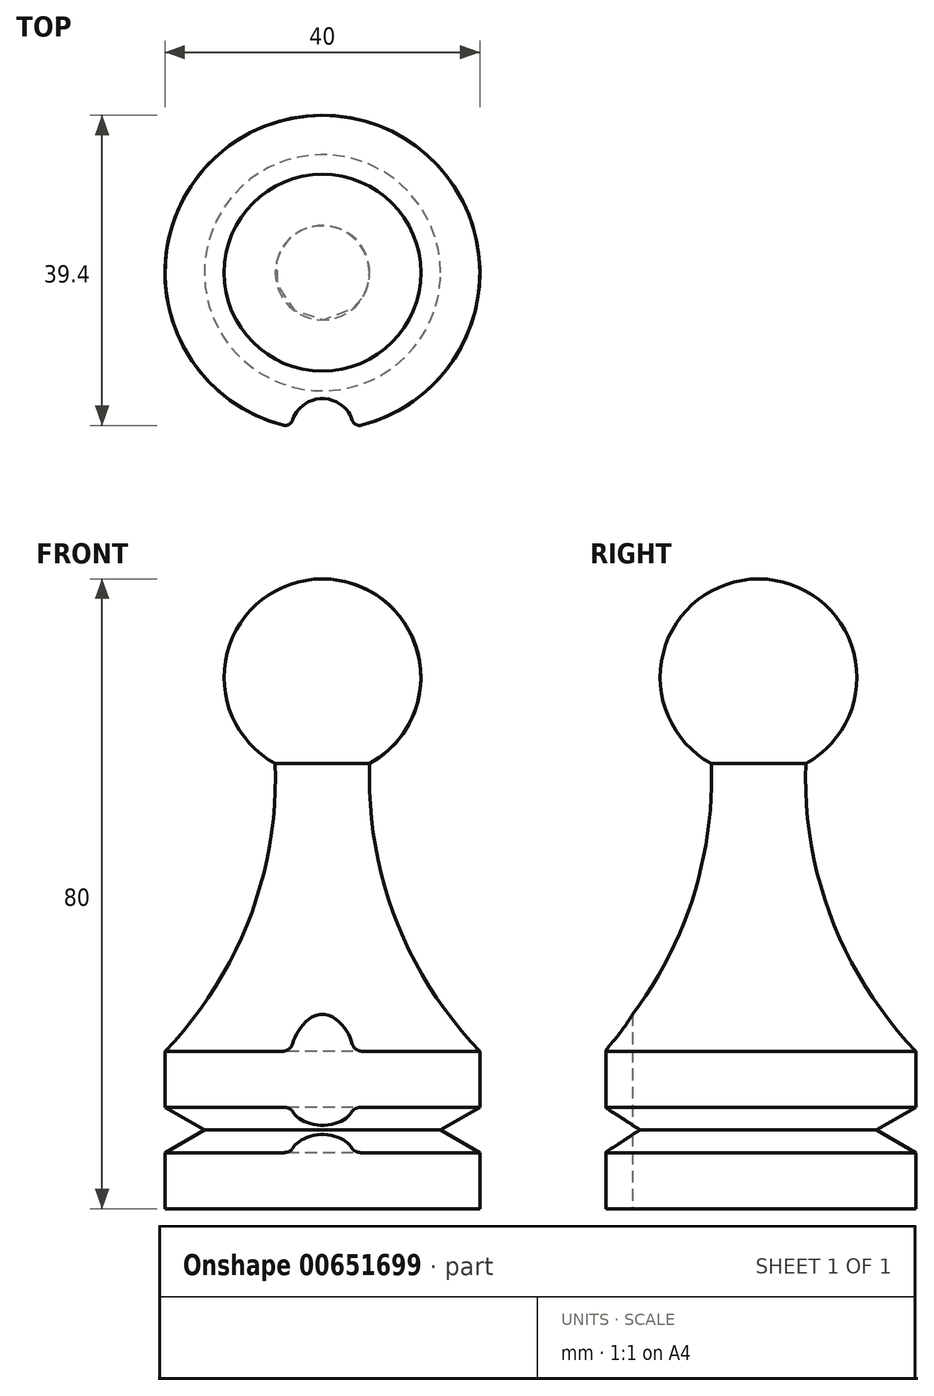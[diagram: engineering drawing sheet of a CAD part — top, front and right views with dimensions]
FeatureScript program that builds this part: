
annotation { "Feature Type Name" : "Feature", "Feature Type Description" : "" }
export const myFeature = defineFeature(function(context is Context, id is Id, definition is map)
    precondition{}
    {
        {
            var Q0;
            Q0=qCreatedBy(makeId("Front.planeOp"),FACE);
            var sketch = newSketch(context, id + "F0", { "sketchPlane" : qUnion([Q0])});
            skLineSegment(sketch, "E0", {"start": v(0, 98.63) * mm, "end": v(0, -34.87) * mm, "construction": true});
            skLineSegment(sketch, "E1", {"start": v(0, 0) * mm, "end": v(20, 0) * mm});
            skLineSegment(sketch, "E2", {"start": v(20, 0) * mm, "end": v(20, 7.11) * mm});
            skLineSegment(sketch, "E3", {"start": v(20, 7.11) * mm, "end": v(15, 10) * mm});
            skLineSegment(sketch, "E4", {"start": v(15, 10) * mm, "end": v(20, 12.89) * mm});
            skLineSegment(sketch, "E5", {"start": v(20, 12.89) * mm, "end": v(20, 20) * mm});
            skArc(sketch, "E6", {"start": v(6, 56.53) * mm, "mid": v(9.28, 36.84) * mm, "end": v(20, 20) * mm});
            skLineSegment(sketch, "E7", {"start": v(0, 80) * mm, "end": v(0, 0) * mm});
            skArc(sketch, "E8", {"start": v(6, 56.53) * mm, "mid": v(12.11, 70.6) * mm, "end": v(0, 80) * mm});
            skSolve(sketch);
        }
        {
            var Q0;
            Q0 = qSketchRegion(id + "F0", true);
            var Q1;
            Q1=sQuery(id+"F0.wireOp",EDGE,"E0");
            revolve(context, id + "F1", {"entities" : qUnion([Q0]), "axis" : qUnion([Q1]), "revolveType" : RevolveType.FULL});
        }
        {
            var Q0;
            Q0=makeQuery(id+"F1.opRevolve","SWEPT_FACE",FACE,{"disambiguationData":[OSD([sQuery(id+"F0.wireOp",EDGE,"E1")])]});
            var sketch = newSketch(context, id + "F2", { "sketchPlane" : qUnion([Q0])});
            skCircle(sketch, "E9", {"center": v(0, 20) * mm, "radius": 4 * mm});
            skSolve(sketch);
        }
        {
            var Q0;
            Q0 = qSketchRegion(id + "F2", true);
            extrude(context, id + "F3", {"entities" : qUnion([Q0]), "operationType" : NewBodyOperationType.REMOVE, "oppositeDirection" : true, "depth" : 30 * mm, "offsetDistance" : 25 * mm});
        }
        {
            var Q0;
            Q0=makeQuery(id+"F3.boolean.opBoolean","INTERSECT",EDGE,{"disambiguationData":[OD(1.0)],"derivedFrom":[makeQuery(id+"F1.opRevolve","SWEPT_FACE",FACE,{"disambiguationData":[OSD([sQuery(id+"F0.wireOp",EDGE,"E5")])]}),makeQuery(id+"F3.opExtrude","SWEPT_FACE",FACE,{"disambiguationData":[OSD([sQuery(id+"F2.wireOp",EDGE,"E9")])]})]});
            var Q1;
            Q1=makeQuery(id+"F3.boolean.opBoolean","INTERSECT",EDGE,{"disambiguationData":[OD(1.0)],"derivedFrom":[makeQuery(id+"F1.opRevolve","SWEPT_FACE",FACE,{"disambiguationData":[OSD([sQuery(id+"F0.wireOp",EDGE,"E2")])]}),makeQuery(id+"F3.opExtrude","SWEPT_FACE",FACE,{"disambiguationData":[OSD([sQuery(id+"F2.wireOp",EDGE,"E9")])]})]});
            var Q2;
            Q2=makeQuery(id+"F3.boolean.opBoolean","INTERSECT",EDGE,{"disambiguationData":[OD(0.0)],"derivedFrom":[makeQuery(id+"F1.opRevolve","SWEPT_FACE",FACE,{"disambiguationData":[OSD([sQuery(id+"F0.wireOp",EDGE,"E2")])]}),makeQuery(id+"F3.opExtrude","SWEPT_FACE",FACE,{"disambiguationData":[OSD([sQuery(id+"F2.wireOp",EDGE,"E9")])]})]});
            var Q3;
            Q3=makeQuery(id+"F3.boolean.opBoolean","INTERSECT",EDGE,{"disambiguationData":[OD(0.0)],"derivedFrom":[makeQuery(id+"F1.opRevolve","SWEPT_FACE",FACE,{"disambiguationData":[OSD([sQuery(id+"F0.wireOp",EDGE,"E5")])]}),makeQuery(id+"F3.opExtrude","SWEPT_FACE",FACE,{"disambiguationData":[OSD([sQuery(id+"F2.wireOp",EDGE,"E9")])]})]});
            fillet(context, id + "F4", {"entities" : qUnion([Q0, Q1, Q2, Q3]), "radius" : 1 * mm, "tangentPropagation" : true, "allowEdgeOverflow" : false});
        }
    });
